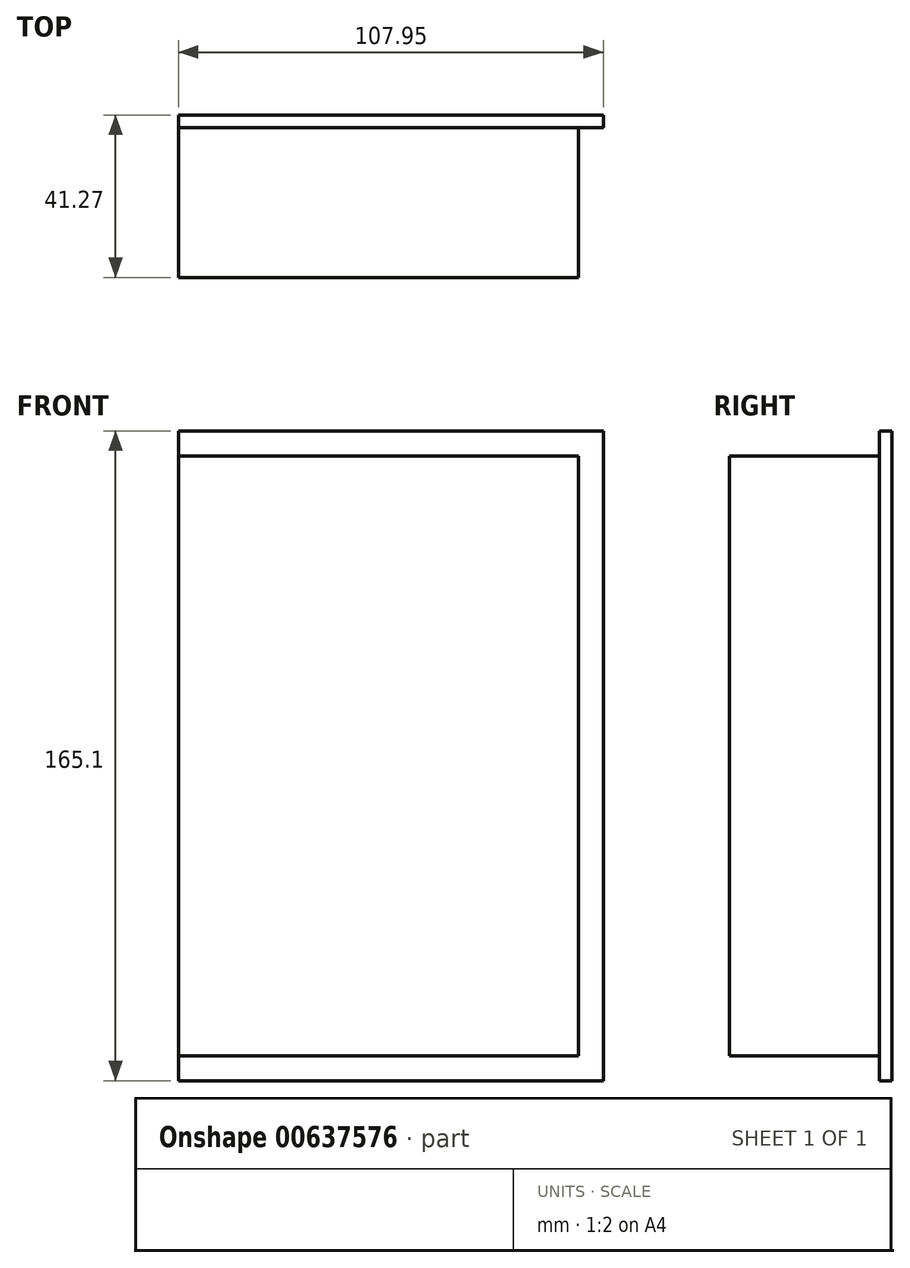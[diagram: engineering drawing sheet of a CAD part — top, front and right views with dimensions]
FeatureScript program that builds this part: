
annotation { "Feature Type Name" : "Feature", "Feature Type Description" : "" }
export const myFeature = defineFeature(function(context is Context, id is Id, definition is map)
    precondition{}
    {
        {
            var Q0;
            Q0=qCreatedBy(makeId("Front.planeOp"),FACE);
            var sketch = newSketch(context, id + "F0", { "sketchPlane" : qUnion([Q0])});
            skLineSegment(sketch, "E0.bottom", {"start": v(0, 0) * mm, "end": v(101.6, 0) * mm});
            skLineSegment(sketch, "E0.top", {"start": v(0, -152.4) * mm, "end": v(101.6, -152.4) * mm});
            skLineSegment(sketch, "E0.left", {"start": v(0, 0) * mm, "end": v(0, -152.4) * mm});
            skLineSegment(sketch, "E0.right", {"start": v(101.6, 0) * mm, "end": v(101.6, -152.4) * mm});
            skSolve(sketch);
        }
        {
            var Q0;
            Q0=makeQuery(id+"F0.imprint","IMPRINT",FACE,{"disambiguationData":[TD([[makeQuery(id+"F0.imprint","IMPRINT",EDGE,{"derivedFrom":sQuery(id+"F0.wireOp",EDGE,"E0.bottom")}),-1.0]])]});
            extrude(context, id + "F1", {"entities" : qUnion([Q0]), "depth" : 38.1 * mm, "offsetDistance" : 25.4 * mm});
        }
        {
            var Q0;
            Q0=makeQuery(id+"F1.opExtrude","CAP_FACE",FACE,{"disambiguationData":[OSD([sQuery(id+"F0.wireOp",EDGE,"E0.bottom"),sQuery(id+"F0.wireOp",EDGE,"E0.top"),sQuery(id+"F0.wireOp",EDGE,"E0.left"),sQuery(id+"F0.wireOp",EDGE,"E0.right")])],"isStart":true});
            var sketch = newSketch(context, id + "F2", { "sketchPlane" : qUnion([Q0])});
            skLineSegment(sketch, "E1.bottom", {"start": v(0, -158.75) * mm, "end": v(-107.95, -158.75) * mm});
            skLineSegment(sketch, "E1.top", {"start": v(0, 6.35) * mm, "end": v(-107.95, 6.35) * mm});
            skLineSegment(sketch, "E1.left", {"start": v(0, -158.75) * mm, "end": v(0, 6.35) * mm});
            skLineSegment(sketch, "E1.right", {"start": v(-107.95, -158.75) * mm, "end": v(-107.95, 6.35) * mm});
            skSolve(sketch);
        }
        {
            var Q0;
            {var subQ1=makeQuery(id+"F1.opExtrude","CAP_EDGE",EDGE,{"disambiguationData":[OSD([sQuery(id+"F0.wireOp",EDGE,"E0.bottom")])],"isStart":true});Q0=makeQuery(id+"F2.imprint","IMPRINT",FACE,{"disambiguationData":[TD([[makeQuery(id+"F2.imprint","IMPRINT",EDGE,{"derivedFrom":subQ1}),1.0]])]});}
            var Q1;
            {var subQ4=sQuery(id+"F2.wireOp",EDGE,"E1.bottom");Q1=makeQuery(id+"F2.imprint","IMPRINT",FACE,{"disambiguationData":[TD([[makeQuery(id+"F2.imprint","IMPRINT",EDGE,{"derivedFrom":subQ4}),-1.0]])]});}
            extrude(context, id + "F3", {"entities" : qUnion([Q0, Q1]), "operationType" : NewBodyOperationType.ADD, "depth" : 3.17 * mm, "offsetDistance" : 25.4 * mm});
        }
    });
